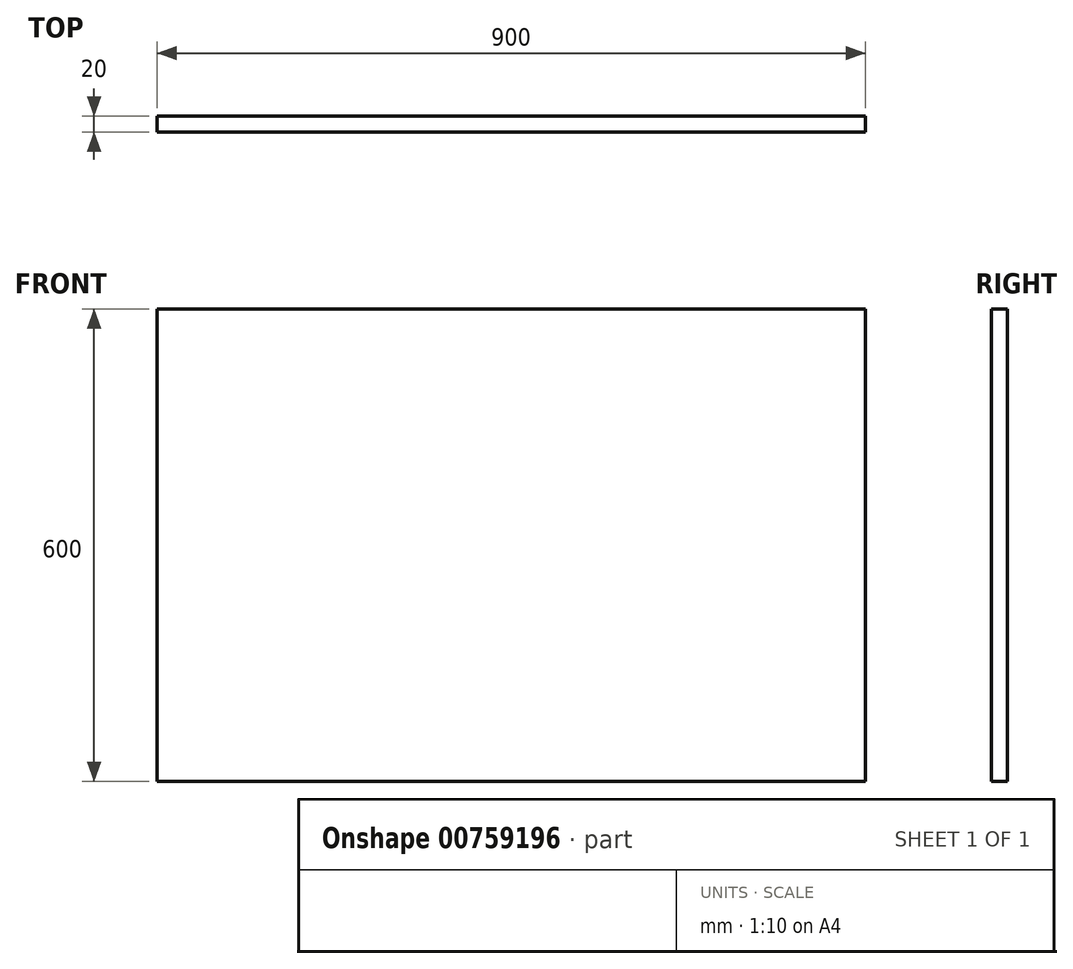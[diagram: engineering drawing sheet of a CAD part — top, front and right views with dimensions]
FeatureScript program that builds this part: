
annotation { "Feature Type Name" : "Feature", "Feature Type Description" : "" }
export const myFeature = defineFeature(function(context is Context, id is Id, definition is map)
    precondition{}
    {
        {
            var Q0;
            Q0=qCreatedBy(makeId("Front.planeOp"),FACE);
            var sketch = newSketch(context, id + "F0", { "sketchPlane" : qUnion([Q0])});
            skLineSegment(sketch, "E0.bottom", {"start": v(0, 0) * mm, "end": v(900, 0) * mm});
            skLineSegment(sketch, "E0.top", {"start": v(0, -600) * mm, "end": v(900, -600) * mm});
            skLineSegment(sketch, "E0.left", {"start": v(0, 0) * mm, "end": v(0, -600) * mm});
            skLineSegment(sketch, "E0.right", {"start": v(900, 0) * mm, "end": v(900, -600) * mm});
            skSolve(sketch);
        }
        {
            var Q0;
            Q0 = qSketchRegion(id + "F0", true);
            extrude(context, id + "F1", {"entities" : qUnion([Q0]), "depth" : 20 * mm, "offsetDistance" : 25 * mm});
        }
    });
